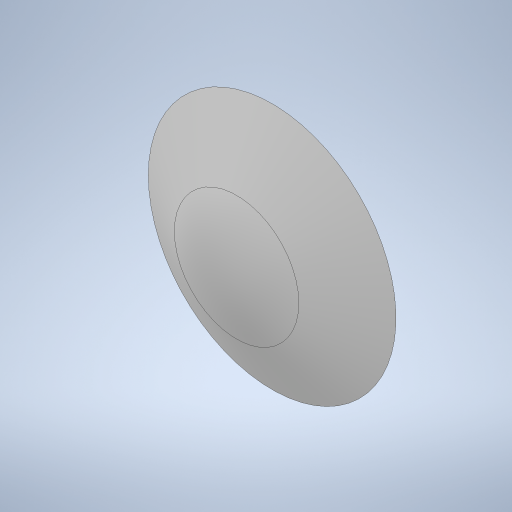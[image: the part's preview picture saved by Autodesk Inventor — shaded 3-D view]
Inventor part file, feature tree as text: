
AUTODESK INVENTOR PART (.ipt)
format: ipt  version: 2023 (Build 270158000, 158)  size: 240,128 bytes
history: native  units: in
note: dims shown in document units (in); Inventor stores cm internally (conversion verified against a paired STEP export)
features: chamfer x1
ambient origin geometry x8: Origin, YZ Plane, XZ Plane, XY Plane, X Axis, Y Axis, Z Axis, Center Point
bodies: Solid1 (feature_tree)
feature tree (1):
  chamfer  "Fase1"  [1 undecoded]
note: 1 required parameter value undecoded (feature->parameter linkage not recoverable at this tier; creation-order binding heuristic only, values carry confidence <= 0.55)
